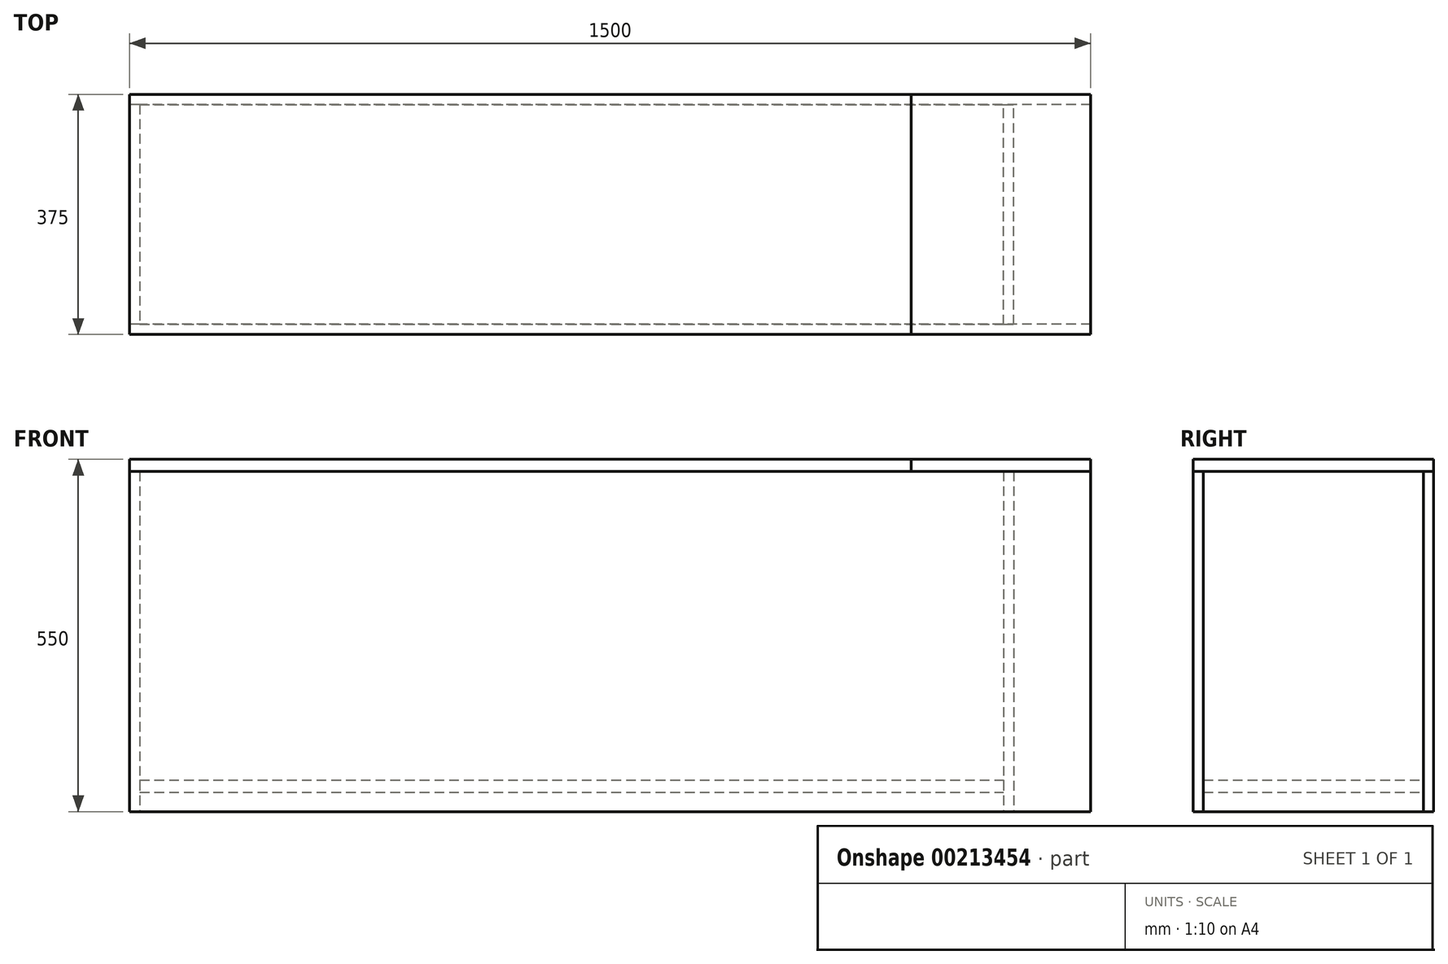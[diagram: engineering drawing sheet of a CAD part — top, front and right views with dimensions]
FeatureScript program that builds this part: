
annotation { "Feature Type Name" : "Feature", "Feature Type Description" : "" }
export const myFeature = defineFeature(function(context is Context, id is Id, definition is map)
    precondition{}
    {
        {
            var Q0;
            Q0=qCreatedBy(makeId("Top.planeOp"),FACE);
            var sketch = newSketch(context, id + "F0", { "sketchPlane" : qUnion([Q0])});
            skLineSegment(sketch, "E0.bottom", {"start": v(0, 0) * mm, "end": v(-1500, 0) * mm});
            skLineSegment(sketch, "E0.top", {"start": v(0, -375) * mm, "end": v(-1500, -375) * mm});
            skLineSegment(sketch, "E0.left", {"start": v(0, 0) * mm, "end": v(0, -375) * mm});
            skLineSegment(sketch, "E0.right", {"start": v(-1500, 0) * mm, "end": v(-1500, -375) * mm});
            skSolve(sketch);
        }
        {
            var Q0;
            Q0 = qSketchRegion(id + "F0", true);
            var Q1;
            Q1=sQuery(id+"F0.wireOp",EDGE,"E0.top");
            var Q2;
            Q2=sQuery(id+"F0.wireOp",EDGE,"E0.right");
            var Q3;
            Q3=sQuery(id+"F0.wireOp",EDGE,"E0.bottom");
            var Q4;
            Q4=sQuery(id+"F0.wireOp",EDGE,"E0.left");
            extrude(context, id + "F1", {"entities" : qUnion([Q0]), "bodyType" : ExtendedToolBodyType.SURFACE, "surfaceEntities" : qUnion([Q1, Q2, Q3, Q4]), "depth" : (550 - 19) * mm});
        }
        {
            var Q0;
            Q0=makeQuery(id+"F1.opExtrude","SWEPT_FACE",FACE,{"disambiguationData":[OSD([sQuery(id+"F0.wireOp",EDGE,"E0.top")])]});
            extrude(context, id + "F2", {"entities" : qUnion([Q0]), "depth" : 16 * mm});
        }
        {
            var Q0;
            Q0=makeQuery(id+"F1.opExtrude","SWEPT_FACE",FACE,{"disambiguationData":[OSD([sQuery(id+"F0.wireOp",EDGE,"E0.bottom")])]});
            extrude(context, id + "F3", {"entities" : qUnion([Q0]), "depth" : 16 * mm});
        }
        {
            var Q0;
            Q0=makeQuery(id+"F1.opExtrude","SWEPT_FACE",FACE,{"disambiguationData":[OSD([sQuery(id+"F0.wireOp",EDGE,"E0.right")])]});
            var sketch = newSketch(context, id + "F4", { "sketchPlane" : qUnion([Q0])});
            skLineSegment(sketch, "E1.bottom", {"start": v(-16, 531) * mm, "end": v(-359, 531) * mm});
            skLineSegment(sketch, "E1.top", {"start": v(-16, 0) * mm, "end": v(-359, 0) * mm});
            skLineSegment(sketch, "E1.left", {"start": v(-16, 531) * mm, "end": v(-16, 0) * mm});
            skLineSegment(sketch, "E1.right", {"start": v(-359, 531) * mm, "end": v(-359, 0) * mm});
            skSolve(sketch);
        }
        {
            var Q0;
            Q0 = qSketchRegion(id + "F4", true);
            extrude(context, id + "F5", {"entities" : qUnion([Q0]), "depth" : 16 * mm});
        }
        {
            var Q0;
            Q0=qCreatedBy(makeId("Right.planeOp"),FACE);
            cPlane(context, id + "F6", {"entities" : qUnion([Q0]), "cplaneType" : CPlaneType.OFFSET, "offset" : 120 * mm, "oppositeDirection" : true, "width" : 150 * mm, "height" : 150 * mm});
        }
        {
            var Q0;
            Q0=qCreatedBy(id+"F6.planeOp",FACE);
            var sketch = newSketch(context, id + "F7", { "sketchPlane" : qUnion([Q0])});
            skLineSegment(sketch, "E2.bottom", {"start": v(-359, 531) * mm, "end": v(-16, 531) * mm});
            skLineSegment(sketch, "E2.top", {"start": v(-359, 0) * mm, "end": v(-16, 0) * mm});
            skLineSegment(sketch, "E2.left", {"start": v(-359, 531) * mm, "end": v(-359, 0) * mm});
            skLineSegment(sketch, "E2.right", {"start": v(-16, 531) * mm, "end": v(-16, 0) * mm});
            skSolve(sketch);
        }
        {
            var Q0;
            Q0=makeQuery(id+"F7.imprint","IMPRINT",FACE,{"disambiguationData":[TD([[makeQuery(id+"F7.imprint","IMPRINT",EDGE,{"derivedFrom":sQuery(id+"F7.wireOp",EDGE,"E2.bottom")}),-1.0]])]});
            extrude(context, id + "F8", {"entities" : qUnion([Q0]), "oppositeDirection" : true, "depth" : 16 * mm});
        }
        {
            var Q0;
            Q0=qCreatedBy(makeId("Top.planeOp"),FACE);
            var Q1;
            Q1=makeQuery(id+"F1.opExtrude","CAP_VERTEX",VERTEX,{"disambiguationData":[OSD([sQuery(id+"F0.wireOp",VERTEX,"E0.left.start")])],"isStart":false});
            cPlane(context, id + "F9", {"entities" : qUnion([Q0, Q1]), "cplaneType" : CPlaneType.PLANE_POINT, "offset" : 25 * mm, "width" : 150 * mm, "height" : 150 * mm});
        }
        {
            var Q0;
            Q0=qCreatedBy(id+"F9.planeOp",FACE);
            var sketch = newSketch(context, id + "F10", { "sketchPlane" : qUnion([Q0])});
            skLineSegment(sketch, "E3.bottom", {"start": v(0, 0) * mm, "end": v(-280, 0) * mm});
            skLineSegment(sketch, "E3.top", {"start": v(0, -375) * mm, "end": v(-280, -375) * mm});
            skLineSegment(sketch, "E3.left", {"start": v(0, 0) * mm, "end": v(0, -375) * mm});
            skLineSegment(sketch, "E3.right", {"start": v(-280, 0) * mm, "end": v(-280, -375) * mm});
            skSolve(sketch);
        }
        {
            var Q0;
            Q0=makeQuery(id+"F10.imprint","IMPRINT",FACE,{"disambiguationData":[TD([[makeQuery(id+"F10.imprint","IMPRINT",EDGE,{"derivedFrom":sQuery(id+"F10.wireOp",EDGE,"E3.bottom")}),1.0]])]});
            extrude(context, id + "F11", {"entities" : qUnion([Q0]), "depth" : 19 * mm});
        }
        {
            var Q0;
            Q0=qCreatedBy(id+"F9.planeOp",FACE);
            var sketch = newSketch(context, id + "F12", { "sketchPlane" : qUnion([Q0])});
            skLineSegment(sketch, "E4.bottom", {"start": v(-1500, 0) * mm, "end": v(-280, 0) * mm});
            skLineSegment(sketch, "E4.top", {"start": v(-1500, -375) * mm, "end": v(-280, -375) * mm});
            skLineSegment(sketch, "E4.left", {"start": v(-1500, 0) * mm, "end": v(-1500, -375) * mm});
            skLineSegment(sketch, "E4.right", {"start": v(-280, 0) * mm, "end": v(-280, -375) * mm});
            skSolve(sketch);
        }
        {
            var Q0;
            Q0=makeQuery(id+"F12.imprint","IMPRINT",FACE,{"disambiguationData":[TD([[makeQuery(id+"F12.imprint","IMPRINT",EDGE,{"derivedFrom":sQuery(id+"F12.wireOp",EDGE,"E4.bottom")}),-1.0]])]});
            extrude(context, id + "F13", {"entities" : qUnion([Q0]), "depth" : 19 * mm});
        }
        {
            var Q0;
            Q0=qCreatedBy(makeId("Top.planeOp"),FACE);
            var sketch = newSketch(context, id + "F14", { "sketchPlane" : qUnion([Q0])});
            skLineSegment(sketch, "E5.bottom", {"start": v(-1484, -359) * mm, "end": v(-136, -359) * mm});
            skLineSegment(sketch, "E5.top", {"start": v(-1484, -16) * mm, "end": v(-136, -16) * mm});
            skLineSegment(sketch, "E5.left", {"start": v(-1484, -359) * mm, "end": v(-1484, -16) * mm});
            skLineSegment(sketch, "E5.right", {"start": v(-136, -359) * mm, "end": v(-136, -16) * mm});
            skSolve(sketch);
        }
        {
            var Q0;
            Q0=makeQuery(id+"F14.imprint","IMPRINT",FACE,{"disambiguationData":[TD([[makeQuery(id+"F14.imprint","IMPRINT",EDGE,{"derivedFrom":sQuery(id+"F14.wireOp",EDGE,"E5.bottom")}),1.0]])]});
            extrude(context, id + "F15", {"entities" : qUnion([Q0]), "depth" : (30 + 19) * mm, "hasSecondDirection" : true, "secondDirectionOppositeDirection" : false, "secondDirectionDepth" : 30 * mm});
        }
    });
